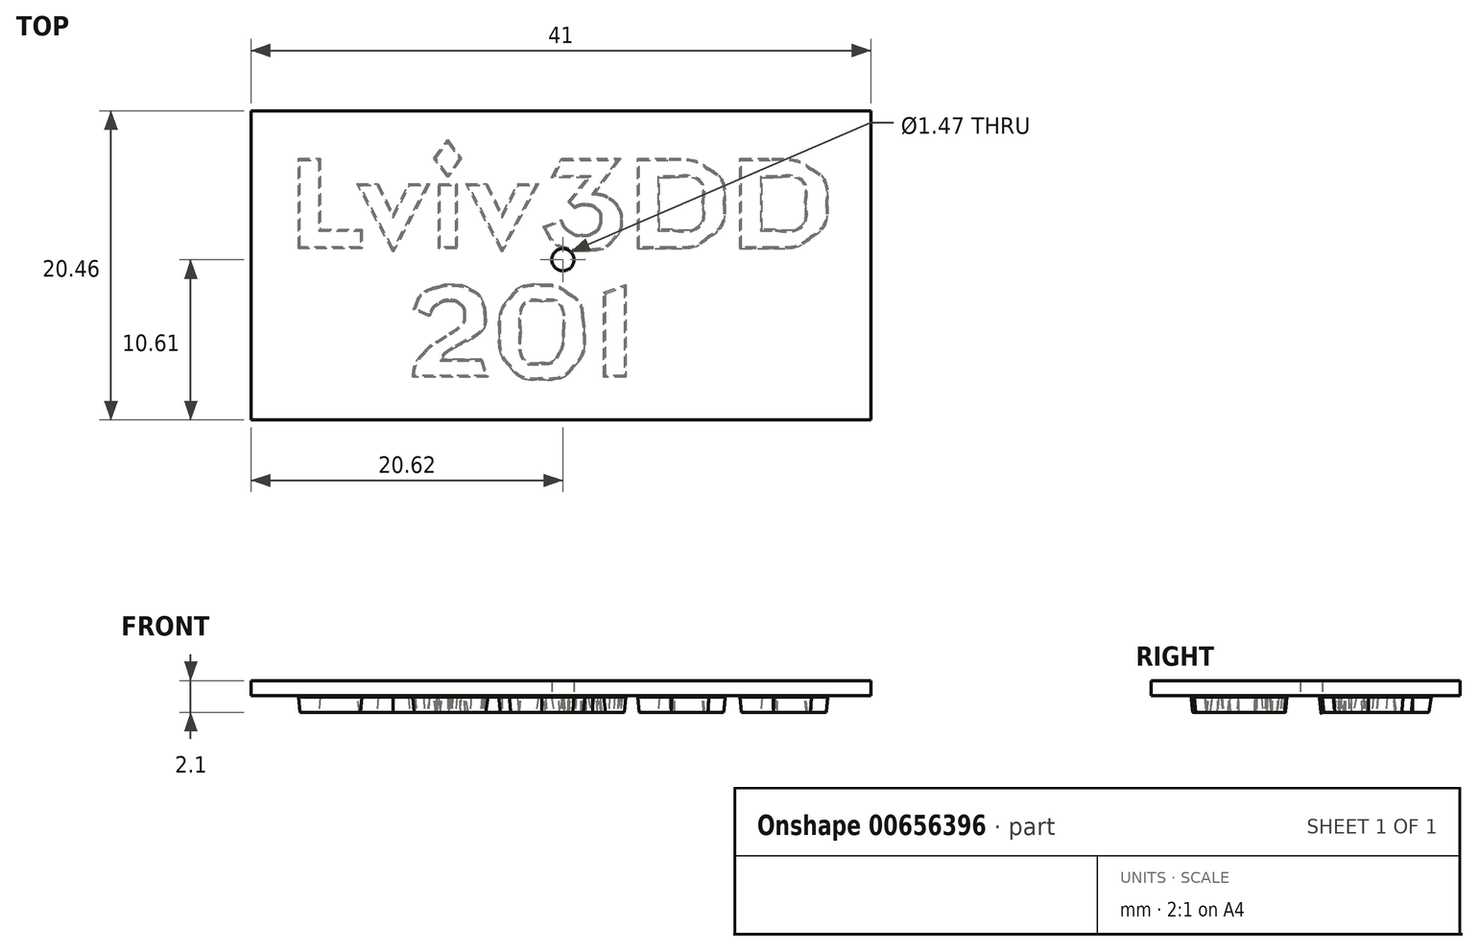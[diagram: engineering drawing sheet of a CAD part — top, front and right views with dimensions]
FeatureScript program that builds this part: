
annotation { "Feature Type Name" : "Feature", "Feature Type Description" : "" }
export const myFeature = defineFeature(function(context is Context, id is Id, definition is map)
    precondition{}
    {
        {
            var Q0;
            Q0=qCreatedBy(makeId("Top.planeOp"),FACE);
            var sketch = newSketch(context, id + "F0", { "sketchPlane" : qUnion([Q0])});
            skLineSegment(sketch, "E0.bottom", {"start": v(-20.62, 9.85) * mm, "end": v(20.38, 9.85) * mm});
            skLineSegment(sketch, "E0.top", {"start": v(-20.62, -10.6) * mm, "end": v(20.38, -10.6) * mm});
            skLineSegment(sketch, "E0.left", {"start": v(-20.62, 9.85) * mm, "end": v(-20.62, -10.6) * mm});
            skLineSegment(sketch, "E0.right", {"start": v(20.38, 9.85) * mm, "end": v(20.38, -10.6) * mm});
            skCircle(sketch, "E1", {"center": v(0, 0) * mm, "radius": 0.73 * mm});
            skSolve(sketch);
        }
        {
            var Q0;
            Q0 = qSketchRegion(id + "F0", true);
            extrude(context, id + "F1", {"entities" : qUnion([Q0]), "depth" : 1 * mm, "offsetDistance" : 25 * mm});
        }
        {
            var Q0;
            Q0=qCreatedBy(makeId("Top.planeOp"),FACE);
            var sketch = newSketch(context, id + "F2", { "sketchPlane" : qUnion([Q0])});
            skFitSpline(sketch, "E2", {"points": [v(14.06, 2) * mm, v(15.36, 2) * mm, v(16.01, 2.6) * mm, v(16.01, 3.79) * mm]});
            skFitSpline(sketch, "E3", {"points": [v(16.01, 3.79) * mm, v(16.01, 4.89) * mm, v(15.4, 5.44) * mm, v(14.2, 5.44) * mm]});
            skLineSegment(sketch, "E4", {"start": v(13.19, 2) * mm, "end": v(14.06, 2) * mm});
            skLineSegment(sketch, "E5", {"start": v(14.2, 5.44) * mm, "end": v(13.19, 5.44) * mm});
            skLineSegment(sketch, "E6", {"start": v(13.19, 5.44) * mm, "end": v(13.19, 2) * mm});
            skFitSpline(sketch, "E7", {"points": [v(13.85, 6.7) * mm, v(14.93, 6.7) * mm, v(15.78, 6.48) * mm, v(16.4, 6.06) * mm]});
            skFitSpline(sketch, "E8", {"points": [v(16.4, 6.06) * mm, v(17.13, 5.57) * mm, v(17.5, 4.8) * mm, v(17.5, 3.77) * mm]});
            skFitSpline(sketch, "E9", {"points": [v(17.5, 3.77) * mm, v(17.5, 2.77) * mm, v(17.15, 2) * mm, v(16.45, 1.47) * mm]});
            skFitSpline(sketch, "E10", {"points": [v(16.45, 1.47) * mm, v(15.82, 0.98) * mm, v(15, 0.74) * mm, v(13.96, 0.74) * mm]});
            skLineSegment(sketch, "E11", {"start": v(11.73, 0.74) * mm, "end": v(11.73, 6.7) * mm});
            skLineSegment(sketch, "E12", {"start": v(11.73, 6.7) * mm, "end": v(13.85, 6.7) * mm});
            skLineSegment(sketch, "E13", {"start": v(13.96, 0.74) * mm, "end": v(11.73, 0.74) * mm});
            skFitSpline(sketch, "E14", {"points": [v(7.27, 2) * mm, v(8.57, 2) * mm, v(9.23, 2.6) * mm, v(9.23, 3.79) * mm]});
            skFitSpline(sketch, "E15", {"points": [v(9.23, 3.79) * mm, v(9.23, 4.89) * mm, v(8.62, 5.44) * mm, v(7.4, 5.44) * mm]});
            skLineSegment(sketch, "E16", {"start": v(6.4, 2) * mm, "end": v(7.27, 2) * mm});
            skLineSegment(sketch, "E17", {"start": v(7.4, 5.44) * mm, "end": v(6.4, 5.44) * mm});
            skLineSegment(sketch, "E18", {"start": v(6.4, 5.44) * mm, "end": v(6.4, 2) * mm});
            skFitSpline(sketch, "E19", {"points": [v(7.06, 6.7) * mm, v(8.14, 6.7) * mm, v(9, 6.48) * mm, v(9.61, 6.06) * mm]});
            skFitSpline(sketch, "E20", {"points": [v(9.61, 6.06) * mm, v(10.35, 5.57) * mm, v(10.71, 4.8) * mm, v(10.71, 3.77) * mm]});
            skFitSpline(sketch, "E21", {"points": [v(10.71, 3.77) * mm, v(10.71, 2.77) * mm, v(10.36, 2) * mm, v(9.66, 1.47) * mm]});
            skFitSpline(sketch, "E22", {"points": [v(9.66, 1.47) * mm, v(9.03, 0.98) * mm, v(8.2, 0.74) * mm, v(7.17, 0.74) * mm]});
            skLineSegment(sketch, "E23", {"start": v(4.94, 0.74) * mm, "end": v(4.94, 6.7) * mm});
            skLineSegment(sketch, "E24", {"start": v(4.94, 6.7) * mm, "end": v(7.06, 6.7) * mm});
            skLineSegment(sketch, "E25", {"start": v(7.17, 0.74) * mm, "end": v(4.94, 0.74) * mm});
            skFitSpline(sketch, "E26", {"points": [v(-0.02, 2.48) * mm, v(0.08, 2.26) * mm, v(0.25, 2.07) * mm, v(0.49, 1.9) * mm]});
            skFitSpline(sketch, "E27", {"points": [v(0.49, 1.9) * mm, v(0.72, 1.74) * mm, v(0.96, 1.66) * mm, v(1.2, 1.66) * mm]});
            skLineSegment(sketch, "E28", {"start": v(-1.28, 2.19) * mm, "end": v(-0.1, 2.66) * mm});
            skLineSegment(sketch, "E29", {"start": v(-0.1, 2.66) * mm, "end": v(-0.02, 2.48) * mm});
            skFitSpline(sketch, "E30", {"points": [v(1.33, 1.66) * mm, v(1.57, 1.66) * mm, v(1.78, 1.71) * mm, v(1.97, 1.81) * mm]});
            skFitSpline(sketch, "E31", {"points": [v(1.97, 1.81) * mm, v(2.19, 1.93) * mm, v(2.34, 2.1) * mm, v(2.42, 2.3) * mm]});
            skLineSegment(sketch, "E32", {"start": v(1.2, 1.66) * mm, "end": v(1.33, 1.66) * mm});
            skFitSpline(sketch, "E33", {"points": [v(2.47, 2.48) * mm, v(2.48, 2.56) * mm, v(2.49, 2.62) * mm, v(2.49, 2.67) * mm]});
            skFitSpline(sketch, "E34", {"points": [v(2.49, 2.67) * mm, v(2.49, 2.93) * mm, v(2.4, 3.14) * mm, v(2.22, 3.3) * mm]});
            skFitSpline(sketch, "E35", {"points": [v(2.22, 3.3) * mm, v(2.05, 3.46) * mm, v(1.82, 3.56) * mm, v(1.55, 3.58) * mm]});
            skFitSpline(sketch, "E36", {"points": [v(1.55, 3.58) * mm, v(1.28, 3.58) * mm, v(1.05, 3.54) * mm, v(0.87, 3.45) * mm]});
            skLineSegment(sketch, "E37", {"start": v(2.42, 2.3) * mm, "end": v(2.47, 2.48) * mm});
            skFitSpline(sketch, "E38", {"points": [v(2.28, 4.39) * mm, v(2.56, 4.36) * mm, v(2.83, 4.26) * mm, v(3.09, 4.1) * mm]});
            skFitSpline(sketch, "E39", {"points": [v(3.09, 4.1) * mm, v(3.35, 3.93) * mm, v(3.55, 3.73) * mm, v(3.68, 3.49) * mm]});
            skFitSpline(sketch, "E40", {"points": [v(3.68, 3.49) * mm, v(3.83, 3.22) * mm, v(3.9, 2.93) * mm, v(3.9, 2.63) * mm]});
            skFitSpline(sketch, "E41", {"points": [v(3.9, 2.63) * mm, v(3.9, 2.18) * mm, v(3.75, 1.77) * mm, v(3.43, 1.39) * mm]});
            skFitSpline(sketch, "E42", {"points": [v(3.43, 1.39) * mm, v(3.07, 0.95) * mm, v(2.58, 0.69) * mm, v(1.98, 0.6) * mm]});
            skFitSpline(sketch, "E43", {"points": [v(1.98, 0.6) * mm, v(1.72, 0.56) * mm, v(1.5, 0.54) * mm, v(1.35, 0.54) * mm]});
            skFitSpline(sketch, "E44", {"points": [v(1.35, 0.54) * mm, v(1.13, 0.54) * mm, v(0.85, 0.54) * mm, v(0.35, 0.67) * mm]});
            skFitSpline(sketch, "E45", {"points": [v(0.35, 0.67) * mm, v(-0.15, 0.81) * mm, v(-0.71, 1.2) * mm, v(-1.15, 1.96) * mm]});
            skLineSegment(sketch, "E46", {"start": v(0.87, 3.45) * mm, "end": v(0.78, 3.4) * mm});
            skLineSegment(sketch, "E47", {"start": v(0.78, 3.4) * mm, "end": v(0.35, 3.8) * mm});
            skLineSegment(sketch, "E48", {"start": v(0.35, 3.8) * mm, "end": v(1.66, 5.44) * mm});
            skLineSegment(sketch, "E49", {"start": v(1.66, 5.44) * mm, "end": v(-0.74, 5.44) * mm});
            skLineSegment(sketch, "E50", {"start": v(-0.74, 5.44) * mm, "end": v(-0.08, 6.7) * mm});
            skLineSegment(sketch, "E51", {"start": v(-0.08, 6.7) * mm, "end": v(3.8, 6.7) * mm});
            skLineSegment(sketch, "E52", {"start": v(3.8, 6.7) * mm, "end": v(2.1, 4.4) * mm});
            skLineSegment(sketch, "E53", {"start": v(2.1, 4.4) * mm, "end": v(2.28, 4.39) * mm});
            skLineSegment(sketch, "E54", {"start": v(-1.15, 1.96) * mm, "end": v(-1.28, 2.19) * mm});
            skLineSegment(sketch, "E55", {"start": v(-6.4, 5.02) * mm, "end": v(-5.02, 5.02) * mm});
            skLineSegment(sketch, "E56", {"start": v(-5.02, 5.02) * mm, "end": v(-4.02, 2.98) * mm});
            skLineSegment(sketch, "E57", {"start": v(-4.02, 2.98) * mm, "end": v(-3, 5.02) * mm});
            skLineSegment(sketch, "E58", {"start": v(-3, 5.02) * mm, "end": v(-1.63, 5.02) * mm});
            skLineSegment(sketch, "E59", {"start": v(-1.63, 5.02) * mm, "end": v(-4.02, 0.53) * mm});
            skLineSegment(sketch, "E60", {"start": v(-4.02, 0.53) * mm, "end": v(-6.4, 5.02) * mm});
            skLineSegment(sketch, "E61", {"start": v(-13.61, 5.02) * mm, "end": v(-12.23, 5.02) * mm});
            skLineSegment(sketch, "E62", {"start": v(-12.23, 5.02) * mm, "end": v(-11.22, 2.98) * mm});
            skLineSegment(sketch, "E63", {"start": v(-11.22, 2.98) * mm, "end": v(-10.2, 5.02) * mm});
            skLineSegment(sketch, "E64", {"start": v(-10.2, 5.02) * mm, "end": v(-8.83, 5.02) * mm});
            skLineSegment(sketch, "E65", {"start": v(-8.83, 5.02) * mm, "end": v(-11.22, 0.53) * mm});
            skLineSegment(sketch, "E66", {"start": v(-11.22, 0.53) * mm, "end": v(-13.61, 5.02) * mm});
            skLineSegment(sketch, "E67", {"start": v(-17.5, 0.74) * mm, "end": v(-17.5, 6.7) * mm});
            skLineSegment(sketch, "E68", {"start": v(-17.5, 6.7) * mm, "end": v(-16.05, 6.7) * mm});
            skLineSegment(sketch, "E69", {"start": v(-16.05, 6.7) * mm, "end": v(-16.05, 2) * mm});
            skLineSegment(sketch, "E70", {"start": v(-16.05, 2) * mm, "end": v(-13.3, 2) * mm});
            skLineSegment(sketch, "E71", {"start": v(-13.3, 2) * mm, "end": v(-13.3, 0.74) * mm});
            skLineSegment(sketch, "E72", {"start": v(-13.3, 0.74) * mm, "end": v(-17.5, 0.74) * mm});
            skLineSegment(sketch, "E73", {"start": v(-8.22, 0.74) * mm, "end": v(-8.22, 5.02) * mm});
            skLineSegment(sketch, "E74", {"start": v(-8.22, 5.02) * mm, "end": v(-7, 5.02) * mm});
            skLineSegment(sketch, "E75", {"start": v(-7, 5.02) * mm, "end": v(-7, 0.74) * mm});
            skLineSegment(sketch, "E76", {"start": v(-7, 0.74) * mm, "end": v(-8.22, 0.74) * mm});
            skFitSpline(sketch, "E77", {"points": [v(-9.94, -7.76) * mm, v(-9.87, -7.15) * mm, v(-9.63, -6.61) * mm, v(-9.22, -6.14) * mm]});
            skFitSpline(sketch, "E78", {"points": [v(-9.22, -6.14) * mm, v(-8.96, -5.85) * mm, v(-8.69, -5.61) * mm, v(-8.4, -5.43) * mm]});
            skLineSegment(sketch, "E79", {"start": v(-8.52, 6.7) * mm, "end": v(-7.6, 7.93) * mm});
            skLineSegment(sketch, "E80", {"start": v(-7.6, 7.93) * mm, "end": v(-6.72, 6.7) * mm});
            skLineSegment(sketch, "E81", {"start": v(-6.72, 6.7) * mm, "end": v(-7.6, 5.45) * mm});
            skLineSegment(sketch, "E82", {"start": v(-7.6, 5.45) * mm, "end": v(-8.52, 6.7) * mm});
            skFitSpline(sketch, "E83", {"points": [v(-7.5, -4.86) * mm, v(-6.87, -4.44) * mm, v(-6.55, -4.03) * mm, v(-6.55, -3.65) * mm]});
            skFitSpline(sketch, "E84", {"points": [v(-6.55, -3.65) * mm, v(-6.55, -3.37) * mm, v(-6.64, -3.15) * mm, v(-6.82, -2.99) * mm]});
            skFitSpline(sketch, "E85", {"points": [v(-6.82, -2.99) * mm, v(-7.01, -2.83) * mm, v(-7.25, -2.75) * mm, v(-7.53, -2.75) * mm]});
            skFitSpline(sketch, "E86", {"points": [v(-7.53, -2.75) * mm, v(-7.81, -2.75) * mm, v(-8.03, -2.85) * mm, v(-8.26, -3) * mm]});
            skFitSpline(sketch, "E87", {"points": [v(-8.26, -3) * mm, v(-8.5, -3.13) * mm, v(-8.63, -3.35) * mm, v(-8.75, -3.6) * mm]});
            skLineSegment(sketch, "E88", {"start": v(-8.4, -5.43) * mm, "end": v(-8.35, -5.41) * mm});
            skLineSegment(sketch, "E89", {"start": v(-8.35, -5.41) * mm, "end": v(-7.5, -4.86) * mm});
            skFitSpline(sketch, "E90", {"points": [v(-9.77, -3.05) * mm, v(-9.44, -2.33) * mm, v(-8.86, -1.94) * mm, v(-8.39, -1.8) * mm]});
            skFitSpline(sketch, "E91", {"points": [v(-8.39, -1.8) * mm, v(-7.9, -1.66) * mm, v(-7.7, -1.63) * mm, v(-7.32, -1.64) * mm]});
            skFitSpline(sketch, "E92", {"points": [v(-7.32, -1.64) * mm, v(-6.88, -1.65) * mm, v(-6.47, -1.75) * mm, v(-6.08, -1.96) * mm]});
            skFitSpline(sketch, "E93", {"points": [v(-6.08, -1.96) * mm, v(-5.64, -2.2) * mm, v(-5.36, -2.6) * mm, v(-5.25, -2.9) * mm]});
            skFitSpline(sketch, "E94", {"points": [v(-5.25, -2.9) * mm, v(-5.14, -3.22) * mm, v(-5.12, -3.45) * mm, v(-5.12, -3.6) * mm]});
            skFitSpline(sketch, "E95", {"points": [v(-5.12, -3.6) * mm, v(-5.12, -4.34) * mm, v(-5.56, -4.95) * mm, v(-6.43, -5.43) * mm]});
            skLineSegment(sketch, "E96", {"start": v(-8.75, -3.6) * mm, "end": v(-8.83, -3.78) * mm});
            skLineSegment(sketch, "E97", {"start": v(-8.83, -3.78) * mm, "end": v(-9.89, -3.3) * mm});
            skLineSegment(sketch, "E98", {"start": v(-9.89, -3.3) * mm, "end": v(-9.77, -3.05) * mm});
            skFitSpline(sketch, "E99", {"points": [v(-7.4, -5.97) * mm, v(-7.7, -6.18) * mm, v(-7.9, -6.38) * mm, v(-7.98, -6.58) * mm]});
            skLineSegment(sketch, "E100", {"start": v(-6.43, -5.43) * mm, "end": v(-7.3, -5.9) * mm});
            skLineSegment(sketch, "E101", {"start": v(-7.3, -5.9) * mm, "end": v(-7.4, -5.97) * mm});
            skFitSpline(sketch, "E102", {"points": [v(-4.22, -4.79) * mm, v(-4.22, -3.84) * mm, v(-3.99, -3.1) * mm, v(-3.52, -2.54) * mm]});
            skFitSpline(sketch, "E103", {"points": [v(-3.52, -2.54) * mm, v(-3.03, -1.95) * mm, v(-2.32, -1.65) * mm, v(-1.4, -1.65) * mm]});
            skFitSpline(sketch, "E104", {"points": [v(-1.4, -1.65) * mm, v(-0.72, -1.65) * mm, v(-0.13, -1.83) * mm, v(0.38, -2.2) * mm]});
            skFitSpline(sketch, "E105", {"points": [v(0.38, -2.2) * mm, v(0.94, -2.59) * mm, v(1.26, -3.1) * mm, v(1.35, -3.73) * mm]});
            skFitSpline(sketch, "E106", {"points": [v(1.35, -3.73) * mm, v(1.41, -4.24) * mm, v(1.44, -4.61) * mm, v(1.44, -4.86) * mm]});
            skFitSpline(sketch, "E107", {"points": [v(1.44, -4.86) * mm, v(1.44, -5.79) * mm, v(1.2, -6.52) * mm, v(0.73, -7.06) * mm]});
            skFitSpline(sketch, "E108", {"points": [v(0.73, -7.06) * mm, v(0.23, -7.64) * mm, v(-0.48, -7.93) * mm, v(-1.4, -7.93) * mm]});
            skFitSpline(sketch, "E109", {"points": [v(-1.4, -7.93) * mm, v(-2.33, -7.93) * mm, v(-3.04, -7.64) * mm, v(-3.53, -7.05) * mm]});
            skFitSpline(sketch, "E110", {"points": [v(-3.53, -7.05) * mm, v(-3.99, -6.5) * mm, v(-4.22, -5.75) * mm, v(-4.22, -4.79) * mm]});
            skLineSegment(sketch, "E111", {"start": v(-7.98, -6.58) * mm, "end": v(-5.37, -6.58) * mm});
            skLineSegment(sketch, "E112", {"start": v(-5.37, -6.58) * mm, "end": v(-4.96, -7.76) * mm});
            skLineSegment(sketch, "E113", {"start": v(-4.96, -7.76) * mm, "end": v(-9.94, -7.76) * mm});
            skFitSpline(sketch, "E114", {"points": [v(-2.77, -4.79) * mm, v(-2.77, -6.13) * mm, v(-2.31, -6.8) * mm, v(-1.4, -6.8) * mm]});
            skFitSpline(sketch, "E115", {"points": [v(-1.4, -6.8) * mm, v(-0.89, -6.8) * mm, v(-0.52, -6.59) * mm, v(-0.28, -6.17) * mm]});
            skFitSpline(sketch, "E116", {"points": [v(-0.28, -6.17) * mm, v(-0.1, -5.84) * mm, v(0, -5.4) * mm, v(0, -4.86) * mm]});
            skFitSpline(sketch, "E117", {"points": [v(0, -4.86) * mm, v(0, -3.47) * mm, v(-0.46, -2.78) * mm, v(-1.4, -2.78) * mm]});
            skFitSpline(sketch, "E118", {"points": [v(-1.4, -2.78) * mm, v(-2.31, -2.78) * mm, v(-2.77, -3.45) * mm, v(-2.77, -4.79) * mm]});
            skLineSegment(sketch, "E119", {"start": v(2.72, -7.76) * mm, "end": v(2.72, -2.16) * mm});
            skLineSegment(sketch, "E120", {"start": v(2.72, -2.16) * mm, "end": v(4.17, -1.65) * mm});
            skLineSegment(sketch, "E121", {"start": v(4.17, -1.65) * mm, "end": v(4.17, -7.76) * mm});
            skLineSegment(sketch, "E122", {"start": v(4.17, -7.76) * mm, "end": v(2.72, -7.76) * mm});
            skFitSpline(sketch, "E123", {"points": [v(9.57, -3.48) * mm, v(8.96, -4.3) * mm, v(8.49, -5.32) * mm, v(8.15, -6.52) * mm]});
            skFitSpline(sketch, "E124", {"points": [v(8.15, -6.52) * mm, v(8.08, -6.8) * mm, v(8.01, -7.05) * mm, v(7.97, -7.28) * mm]});
            skLineSegment(sketch, "E125", {"start": v(5.17, -3.07) * mm, "end": v(5.5, -1.81) * mm});
            skLineSegment(sketch, "E126", {"start": v(5.5, -1.81) * mm, "end": v(9.94, -1.81) * mm});
            skLineSegment(sketch, "E127", {"start": v(9.94, -1.81) * mm, "end": v(9.94, -2.97) * mm});
            skLineSegment(sketch, "E128", {"start": v(9.94, -2.97) * mm, "end": v(9.57, -3.48) * mm});
            skFitSpline(sketch, "E129", {"points": [v(6.41, -7.44) * mm, v(6.57, -6.4) * mm, v(6.8, -5.88) * mm, v(7.29, -4.92) * mm]});
            skFitSpline(sketch, "E130", {"points": [v(7.29, -4.92) * mm, v(7.78, -3.97) * mm, v(7.67, -4.15) * mm, v(8.4, -3.07) * mm]});
            skLineSegment(sketch, "E131", {"start": v(7.97, -7.28) * mm, "end": v(7.88, -7.76) * mm});
            skLineSegment(sketch, "E132", {"start": v(7.88, -7.76) * mm, "end": v(6.36, -7.76) * mm});
            skLineSegment(sketch, "E133", {"start": v(6.36, -7.76) * mm, "end": v(6.41, -7.44) * mm});
            skLineSegment(sketch, "E134", {"start": v(8.4, -3.07) * mm, "end": v(5.17, -3.07) * mm});
            skSolve(sketch);
        }
        {
            var Q0;
            Q0 = qSketchRegion(id + "F2", true);
            extrude(context, id + "F3", {"entities" : qUnion([Q0]), "operationType" : NewBodyOperationType.ADD, "oppositeDirection" : true, "depth" : 1.1 * mm, "offsetDistance" : 25 * mm});
        }
        {
            var Q0;
            Q0=makeQuery(id+"F3.opExtrude","CAP_FACE",FACE,{"disambiguationData":[OSD([sQuery(id+"F2.wireOp",EDGE,"E67"),sQuery(id+"F2.wireOp",EDGE,"E68"),sQuery(id+"F2.wireOp",EDGE,"E69"),sQuery(id+"F2.wireOp",EDGE,"E70"),sQuery(id+"F2.wireOp",EDGE,"E71"),sQuery(id+"F2.wireOp",EDGE,"E72")])],"isStart":false});
            var Q1;
            Q1=makeQuery(id+"F3.opExtrude","CAP_FACE",FACE,{"disambiguationData":[OSD([sQuery(id+"F2.wireOp",EDGE,"E61"),sQuery(id+"F2.wireOp",EDGE,"E62"),sQuery(id+"F2.wireOp",EDGE,"E63"),sQuery(id+"F2.wireOp",EDGE,"E64"),sQuery(id+"F2.wireOp",EDGE,"E65"),sQuery(id+"F2.wireOp",EDGE,"E66")])],"isStart":false});
            var Q2;
            Q2=makeQuery(id+"F3.opExtrude","CAP_FACE",FACE,{"disambiguationData":[OSD([sQuery(id+"F2.wireOp",EDGE,"E73"),sQuery(id+"F2.wireOp",EDGE,"E74"),sQuery(id+"F2.wireOp",EDGE,"E75"),sQuery(id+"F2.wireOp",EDGE,"E76")])],"isStart":false});
            var Q3;
            Q3=makeQuery(id+"F3.opExtrude","CAP_FACE",FACE,{"disambiguationData":[OSD([sQuery(id+"F2.wireOp",EDGE,"E79"),sQuery(id+"F2.wireOp",EDGE,"E80"),sQuery(id+"F2.wireOp",EDGE,"E81"),sQuery(id+"F2.wireOp",EDGE,"E82")])],"isStart":false});
            var Q4;
            Q4=makeQuery(id+"F3.opExtrude","CAP_FACE",FACE,{"disambiguationData":[OSD([sQuery(id+"F2.wireOp",EDGE,"E55"),sQuery(id+"F2.wireOp",EDGE,"E56"),sQuery(id+"F2.wireOp",EDGE,"E57"),sQuery(id+"F2.wireOp",EDGE,"E58"),sQuery(id+"F2.wireOp",EDGE,"E59"),sQuery(id+"F2.wireOp",EDGE,"E60")])],"isStart":false});
            var Q5;
            Q5=makeQuery(id+"F3.opExtrude","CAP_FACE",FACE,{"disambiguationData":[OSD([sQuery(id+"F2.wireOp",EDGE,"E26"),sQuery(id+"F2.wireOp",EDGE,"E27"),sQuery(id+"F2.wireOp",EDGE,"E28"),sQuery(id+"F2.wireOp",EDGE,"E29"),sQuery(id+"F2.wireOp",EDGE,"E30"),sQuery(id+"F2.wireOp",EDGE,"E31"),sQuery(id+"F2.wireOp",EDGE,"E32"),sQuery(id+"F2.wireOp",EDGE,"E33"),sQuery(id+"F2.wireOp",EDGE,"E34"),sQuery(id+"F2.wireOp",EDGE,"E35"),sQuery(id+"F2.wireOp",EDGE,"E36"),sQuery(id+"F2.wireOp",EDGE,"E37"),sQuery(id+"F2.wireOp",EDGE,"E38"),sQuery(id+"F2.wireOp",EDGE,"E39"),sQuery(id+"F2.wireOp",EDGE,"E40"),sQuery(id+"F2.wireOp",EDGE,"E41"),sQuery(id+"F2.wireOp",EDGE,"E42"),sQuery(id+"F2.wireOp",EDGE,"E43"),sQuery(id+"F2.wireOp",EDGE,"E44"),sQuery(id+"F2.wireOp",EDGE,"E45"),sQuery(id+"F2.wireOp",EDGE,"E46"),sQuery(id+"F2.wireOp",EDGE,"E47"),sQuery(id+"F2.wireOp",EDGE,"E48"),sQuery(id+"F2.wireOp",EDGE,"E49"),sQuery(id+"F2.wireOp",EDGE,"E50"),sQuery(id+"F2.wireOp",EDGE,"E51"),sQuery(id+"F2.wireOp",EDGE,"E52"),sQuery(id+"F2.wireOp",EDGE,"E53"),sQuery(id+"F2.wireOp",EDGE,"E54")])],"isStart":false});
            var Q6;
            Q6=makeQuery(id+"F3.opExtrude","CAP_FACE",FACE,{"disambiguationData":[OSD([sQuery(id+"F2.wireOp",EDGE,"E14"),sQuery(id+"F2.wireOp",EDGE,"E15"),sQuery(id+"F2.wireOp",EDGE,"E16"),sQuery(id+"F2.wireOp",EDGE,"E17"),sQuery(id+"F2.wireOp",EDGE,"E18"),sQuery(id+"F2.wireOp",EDGE,"E19"),sQuery(id+"F2.wireOp",EDGE,"E20"),sQuery(id+"F2.wireOp",EDGE,"E21"),sQuery(id+"F2.wireOp",EDGE,"E22"),sQuery(id+"F2.wireOp",EDGE,"E23"),sQuery(id+"F2.wireOp",EDGE,"E24"),sQuery(id+"F2.wireOp",EDGE,"E25")])],"isStart":false});
            var Q7;
            Q7=makeQuery(id+"F3.opExtrude","CAP_FACE",FACE,{"disambiguationData":[OSD([sQuery(id+"F2.wireOp",EDGE,"E2"),sQuery(id+"F2.wireOp",EDGE,"E3"),sQuery(id+"F2.wireOp",EDGE,"E4"),sQuery(id+"F2.wireOp",EDGE,"E5"),sQuery(id+"F2.wireOp",EDGE,"E6"),sQuery(id+"F2.wireOp",EDGE,"E7"),sQuery(id+"F2.wireOp",EDGE,"E8"),sQuery(id+"F2.wireOp",EDGE,"E9"),sQuery(id+"F2.wireOp",EDGE,"E10"),sQuery(id+"F2.wireOp",EDGE,"E11"),sQuery(id+"F2.wireOp",EDGE,"E12"),sQuery(id+"F2.wireOp",EDGE,"E13")])],"isStart":false});
            var Q8;
            Q8=makeQuery(id+"F3.opExtrude","CAP_FACE",FACE,{"disambiguationData":[OSD([sQuery(id+"F2.wireOp",EDGE,"E77"),sQuery(id+"F2.wireOp",EDGE,"E78"),sQuery(id+"F2.wireOp",EDGE,"E83"),sQuery(id+"F2.wireOp",EDGE,"E84"),sQuery(id+"F2.wireOp",EDGE,"E85"),sQuery(id+"F2.wireOp",EDGE,"E86"),sQuery(id+"F2.wireOp",EDGE,"E87"),sQuery(id+"F2.wireOp",EDGE,"E88"),sQuery(id+"F2.wireOp",EDGE,"E89"),sQuery(id+"F2.wireOp",EDGE,"E90"),sQuery(id+"F2.wireOp",EDGE,"E91"),sQuery(id+"F2.wireOp",EDGE,"E92"),sQuery(id+"F2.wireOp",EDGE,"E93"),sQuery(id+"F2.wireOp",EDGE,"E94"),sQuery(id+"F2.wireOp",EDGE,"E95"),sQuery(id+"F2.wireOp",EDGE,"E96"),sQuery(id+"F2.wireOp",EDGE,"E97"),sQuery(id+"F2.wireOp",EDGE,"E98"),sQuery(id+"F2.wireOp",EDGE,"E99"),sQuery(id+"F2.wireOp",EDGE,"E100"),sQuery(id+"F2.wireOp",EDGE,"E101"),sQuery(id+"F2.wireOp",EDGE,"E111"),sQuery(id+"F2.wireOp",EDGE,"E112"),sQuery(id+"F2.wireOp",EDGE,"E113")])],"isStart":false});
            var Q9;
            Q9=makeQuery(id+"F3.opExtrude","CAP_FACE",FACE,{"disambiguationData":[OSD([sQuery(id+"F2.wireOp",EDGE,"E102"),sQuery(id+"F2.wireOp",EDGE,"E103"),sQuery(id+"F2.wireOp",EDGE,"E104"),sQuery(id+"F2.wireOp",EDGE,"E105"),sQuery(id+"F2.wireOp",EDGE,"E106"),sQuery(id+"F2.wireOp",EDGE,"E107"),sQuery(id+"F2.wireOp",EDGE,"E108"),sQuery(id+"F2.wireOp",EDGE,"E109"),sQuery(id+"F2.wireOp",EDGE,"E110"),sQuery(id+"F2.wireOp",EDGE,"E114"),sQuery(id+"F2.wireOp",EDGE,"E115"),sQuery(id+"F2.wireOp",EDGE,"E116"),sQuery(id+"F2.wireOp",EDGE,"E117"),sQuery(id+"F2.wireOp",EDGE,"E118")])],"isStart":false});
            var Q10;
            Q10=makeQuery(id+"F3.opExtrude","CAP_FACE",FACE,{"disambiguationData":[OSD([sQuery(id+"F2.wireOp",EDGE,"E119"),sQuery(id+"F2.wireOp",EDGE,"E120"),sQuery(id+"F2.wireOp",EDGE,"E121"),sQuery(id+"F2.wireOp",EDGE,"E122")])],"isStart":false});
            var Q11;
            Q11=makeQuery(id+"F3.opExtrude","CAP_FACE",FACE,{"disambiguationData":[OSD([sQuery(id+"F2.wireOp",EDGE,"E123"),sQuery(id+"F2.wireOp",EDGE,"E124"),sQuery(id+"F2.wireOp",EDGE,"E125"),sQuery(id+"F2.wireOp",EDGE,"E126"),sQuery(id+"F2.wireOp",EDGE,"E127"),sQuery(id+"F2.wireOp",EDGE,"E128"),sQuery(id+"F2.wireOp",EDGE,"E129"),sQuery(id+"F2.wireOp",EDGE,"E130"),sQuery(id+"F2.wireOp",EDGE,"E131"),sQuery(id+"F2.wireOp",EDGE,"E132"),sQuery(id+"F2.wireOp",EDGE,"E133"),sQuery(id+"F2.wireOp",EDGE,"E134")])],"isStart":false});
            chamfer(context, id + "F4", {"entities" : qUnion([Q0, Q1, Q2, Q3, Q4, Q5, Q6, Q7, Q8, Q9, Q10, Q11]), "chamferType" : ChamferType.TWO_OFFSETS, "width1" : 0.1 * mm, "oppositeDirection" : false, "width2" : 1 * mm, "tangentPropagation" : true});
        }
    });
